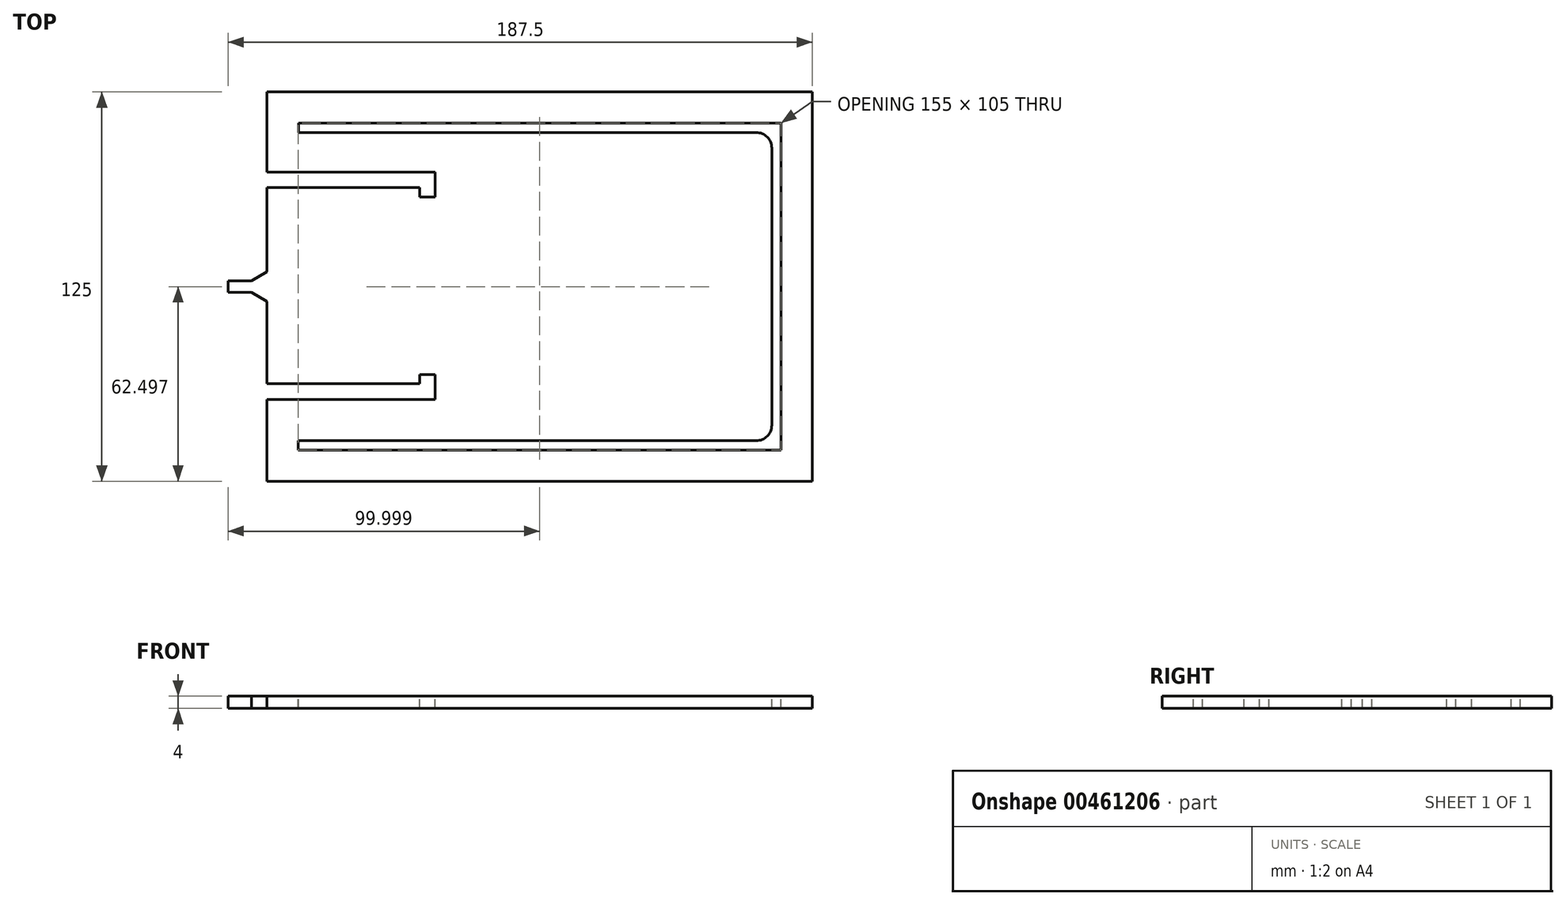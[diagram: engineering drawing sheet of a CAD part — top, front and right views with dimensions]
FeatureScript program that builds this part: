
annotation { "Feature Type Name" : "Feature", "Feature Type Description" : "" }
export const myFeature = defineFeature(function(context is Context, id is Id, definition is map)
    precondition{}
    {
        {
            var Q0;
            Q0=qCreatedBy(makeId("Top.planeOp"),FACE);
            var sketch = newSketch(context, id + "F0", { "sketchPlane" : qUnion([Q0])});
            skLineSegment(sketch, "E0.bottom", {"start": v(100, 75) * mm, "end": v(-100, 75) * mm});
            skLineSegment(sketch, "E0.top", {"start": v(100, -75) * mm, "end": v(-100, -75) * mm});
            skLineSegment(sketch, "E0.left", {"start": v(100, 75) * mm, "end": v(100, -75) * mm});
            skLineSegment(sketch, "E0.right", {"start": v(-100, 75) * mm, "end": v(-100, -75) * mm});
            skPoint(sketch, "E0.middle", {"position": v(0, 0) * mm});
            skSolve(sketch);
        }
        {
            var Q0;
            Q0=makeQuery(id+"F0.imprint","IMPRINT",FACE,{"disambiguationData":[TD([[makeQuery(id+"F0.imprint","IMPRINT",EDGE,{"derivedFrom":sQuery(id+"F0.wireOp",EDGE,"E0.bottom")}),1.0]])]});
            extrude(context, id + "F1", {"entities" : qUnion([Q0]), "depth" : 4 * mm, "offsetDistance" : 25 * mm});
        }
        {
            var Q0;
            Q0=makeQuery(id+"F1.opExtrude","CAP_FACE",FACE,{"disambiguationData":[OSD([sQuery(id+"F0.wireOp",EDGE,"E0.bottom"),sQuery(id+"F0.wireOp",EDGE,"E0.top"),sQuery(id+"F0.wireOp",EDGE,"E0.left"),sQuery(id+"F0.wireOp",EDGE,"E0.right")])],"isStart":false});
            var sketch = newSketch(context, id + "F2", { "sketchPlane" : qUnion([Q0])});
            skLineSegment(sketch, "E1.bottom", {"start": v(87.5, 60.44) * mm, "end": v(-87.5, 60.44) * mm});
            skLineSegment(sketch, "E1.top", {"start": v(87.5, -64.56) * mm, "end": v(-77.5, -64.56) * mm});
            skLineSegment(sketch, "E1.left", {"start": v(87.5, 60.44) * mm, "end": v(87.5, -64.56) * mm});
            skLineSegment(sketch, "E1.right", {"start": v(-87.5, 60.44) * mm, "end": v(-87.5, 34.72) * mm});
            skPoint(sketch, "E1.middle", {"position": v(0, -2.06) * mm});
            skLineSegment(sketch, "E2.bottom", {"start": v(-87.5, 29.72) * mm, "end": v(-46, 29.72) * mm});
            skLineSegment(sketch, "E3", {"start": v(-46, -38.28) * mm, "end": v(-87.5, -38.28) * mm});
            skLineSegment(sketch, "E4", {"start": v(-41, -38.28) * mm, "end": v(-46, -38.28) * mm});
            skLineSegment(sketch, "E5", {"start": v(-41, 34.72) * mm, "end": v(-87.5, 34.72) * mm});
            skLineSegment(sketch, "E6.trimOffspring", {"start": v(-87.5, -38.28) * mm, "end": v(-87.5, -64.56) * mm});
            skLineSegment(sketch, "E7", {"start": v(-6, -30.28) * mm, "end": v(-6, 26.72) * mm});
            skLineSegment(sketch, "E8", {"start": v(-74.36, 50.44) * mm, "end": v(60.64, 50.44) * mm});
            skLineSegment(sketch, "E9", {"start": v(60.64, 47.44) * mm, "end": v(-74.36, 47.44) * mm});
            skLineSegment(sketch, "E10", {"start": v(-74.36, 50.44) * mm, "end": v(-77.36, 50.44) * mm});
            skLineSegment(sketch, "E11", {"start": v(-77.36, 50.44) * mm, "end": v(-77.36, 47.44) * mm});
            skLineSegment(sketch, "E12", {"start": v(-77.36, 47.44) * mm, "end": v(-74.36, 47.44) * mm});
            skLineSegment(sketch, "E13", {"start": v(-87.5, -64.56) * mm, "end": v(-77.5, -64.56) * mm});
            skLineSegment(sketch, "E14", {"start": v(-77.5, -54.56) * mm, "end": v(60.64, -54.56) * mm});
            skLineSegment(sketch, "E15", {"start": v(60.64, -51.56) * mm, "end": v(-77.5, -51.56) * mm});
            skLineSegment(sketch, "E16", {"start": v(-77.5, -54.56) * mm, "end": v(-77.5, -51.56) * mm});
            skLineSegment(sketch, "E17", {"start": v(60.64, 47.44) * mm, "end": v(57.64, 47.44) * mm});
            skLineSegment(sketch, "E18", {"start": v(60.64, 50.44) * mm, "end": v(77.5, 50.44) * mm});
            skLineSegment(sketch, "E19", {"start": v(77.5, 50.44) * mm, "end": v(77.5, -54.56) * mm});
            skLineSegment(sketch, "E20", {"start": v(77.5, -54.56) * mm, "end": v(60.64, -54.56) * mm});
            skLineSegment(sketch, "E21", {"start": v(77.5, 50.44) * mm, "end": v(77.5, 47.44) * mm});
            skLineSegment(sketch, "E22", {"start": v(69.5, 47.44) * mm, "end": v(60.64, 47.44) * mm});
            skLineSegment(sketch, "E23", {"start": v(77.5, 50.44) * mm, "end": v(74.5, 50.44) * mm});
            skLineSegment(sketch, "E24", {"start": v(74.5, 42.44) * mm, "end": v(74.5, -46.56) * mm});
            skLineSegment(sketch, "E25", {"start": v(60.64, -51.56) * mm, "end": v(69.5, -51.56) * mm});
            skPoint(sketch, "E26.end.orphan", {"position": v(77.5, 48.67) * mm});
            skArc(sketch, "E27.filletArc", {"start": v(74.5, 42.44) * mm, "mid": v(73.03, 45.97) * mm, "end": v(69.5, 47.44) * mm});
            skPoint(sketch, "E28.visualSharp", {"position": v(74.5, -51.56) * mm});
            skArc(sketch, "E28.filletArc", {"start": v(69.5, -51.56) * mm, "mid": v(73.03, -50.1) * mm, "end": v(74.5, -46.56) * mm});
            skLineSegment(sketch, "E29", {"start": v(-87.5, 29.72) * mm, "end": v(-38.5, 29.72) * mm});
            skLineSegment(sketch, "E30", {"start": v(-38.5, 29.72) * mm, "end": v(-38.5, 26.72) * mm});
            skLineSegment(sketch, "E31", {"start": v(-38.5, 26.72) * mm, "end": v(-33.5, 26.72) * mm});
            skLineSegment(sketch, "E32", {"start": v(-33.5, 26.72) * mm, "end": v(-33.5, 34.72) * mm});
            skLineSegment(sketch, "E33", {"start": v(-33.5, 34.72) * mm, "end": v(-41, 34.72) * mm});
            skLineSegment(sketch, "E34", {"start": v(-100, -0.26) * mm, "end": v(-100, -3.86) * mm});
            skLineSegment(sketch, "E35", {"start": v(-100, -0.26) * mm, "end": v(-92.5, -0.26) * mm});
            skLineSegment(sketch, "E36", {"start": v(-100, -3.86) * mm, "end": v(-92.5, -3.86) * mm});
            skLineSegment(sketch, "E37", {"start": v(-87.5, -6.86) * mm, "end": v(-92.5, -3.86) * mm});
            skLineSegment(sketch, "E38", {"start": v(-92.5, -0.26) * mm, "end": v(-87.5, 2.74) * mm});
            skLineSegment(sketch, "E39", {"start": v(-87.5, 2.74) * mm, "end": v(-87.5, 29.72) * mm});
            skLineSegment(sketch, "E40", {"start": v(-87.5, -6.86) * mm, "end": v(-87.5, -33.28) * mm});
            skLineSegment(sketch, "E41", {"start": v(-87.5, -33.28) * mm, "end": v(-38.5, -33.28) * mm});
            skLineSegment(sketch, "E42", {"start": v(-38.5, -33.28) * mm, "end": v(-38.5, -30.28) * mm});
            skLineSegment(sketch, "E43", {"start": v(-38.5, -30.28) * mm, "end": v(-33.5, -30.28) * mm});
            skLineSegment(sketch, "E44", {"start": v(-33.5, -30.28) * mm, "end": v(-33.5, -38.28) * mm});
            skLineSegment(sketch, "E45", {"start": v(-33.5, -38.28) * mm, "end": v(-41, -38.28) * mm});
            skPoint(sketch, "E46.start.orphan", {"position": v(-41, -30.28) * mm});
            skLineSegment(sketch, "E47", {"start": v(0, -2.06) * mm, "end": v(40, -2.06) * mm});
            skLineSegment(sketch, "E48", {"start": v(40, -2.06) * mm, "end": v(40, 35.44) * mm});
            skLineSegment(sketch, "E49", {"start": v(40, -2.06) * mm, "end": v(40, -39.56) * mm});
            skPoint(sketch, "E50.end.orphan", {"position": v(42.97, -39.56) * mm});
            skLineSegment(sketch, "E51", {"start": v(40, 35.44) * mm, "end": v(50, 35.44) * mm});
            skLineSegment(sketch, "E52", {"start": v(50, 35.44) * mm, "end": v(50, -39.56) * mm});
            skLineSegment(sketch, "E53", {"start": v(50, -39.56) * mm, "end": v(40, -39.56) * mm});
            skLineSegment(sketch, "E54", {"start": v(40, -2.06) * mm, "end": v(40, 22.94) * mm});
            skLineSegment(sketch, "E55", {"start": v(40, 22.94) * mm, "end": v(50, 22.94) * mm});
            skLineSegment(sketch, "E56", {"start": v(40, -2.06) * mm, "end": v(40, -27.06) * mm});
            skLineSegment(sketch, "E57", {"start": v(40, -27.06) * mm, "end": v(50, -27.06) * mm});
            skSolve(sketch);
        }
        {
            var Q0;
            Q0=makeQuery(id+"F2.imprint","IMPRINT",FACE,{"disambiguationData":[TD([[makeQuery(id+"F2.imprint","IMPRINT",EDGE,{"derivedFrom":sQuery(id+"F2.wireOp",EDGE,"E1.bottom")}),-1.0]])]});
            var Q1;
            Q1=makeQuery(id+"F2.imprint","IMPRINT",FACE,{"disambiguationData":[TD([[makeQuery(id+"F2.imprint","IMPRINT",EDGE,{"derivedFrom":sQuery(id+"F2.wireOp",EDGE,"E8")}),-1.0]])]});
            extrude(context, id + "F3", {"entities" : qUnion([Q0, Q1]), "operationType" : NewBodyOperationType.REMOVE, "oppositeDirection" : true, "depth" : 25 * mm, "offsetDistance" : 25 * mm});
        }
    });
